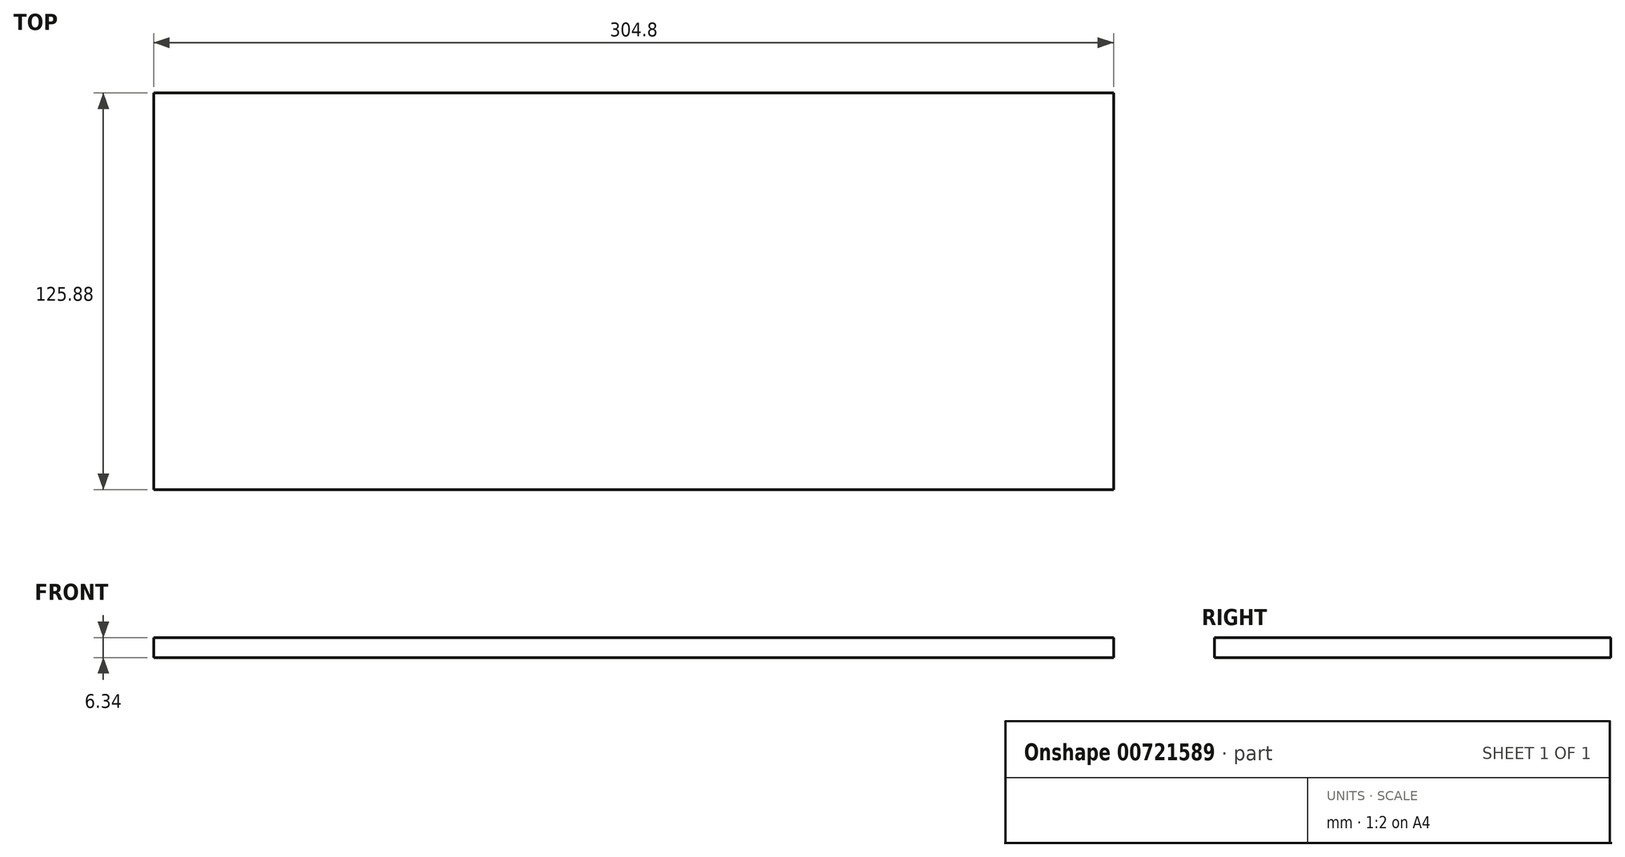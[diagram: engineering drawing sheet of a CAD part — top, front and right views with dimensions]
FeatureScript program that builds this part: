
annotation { "Feature Type Name" : "Feature", "Feature Type Description" : "" }
export const myFeature = defineFeature(function(context is Context, id is Id, definition is map)
    precondition{}
    {
        {
            var Q0;
            Q0=qCreatedBy(makeId("Top.planeOp"),FACE);
            var sketch = newSketch(context, id + "F0", { "sketchPlane" : qUnion([Q0])});
            skLineSegment(sketch, "E0.bottom", {"start": v(152.4, -62.94) * mm, "end": v(-152.4, -62.94) * mm});
            skLineSegment(sketch, "E0.top", {"start": v(152.4, 62.94) * mm, "end": v(-152.4, 62.94) * mm});
            skLineSegment(sketch, "E0.left", {"start": v(152.4, -62.94) * mm, "end": v(152.4, 62.94) * mm});
            skLineSegment(sketch, "E0.right", {"start": v(-152.4, -62.94) * mm, "end": v(-152.4, 62.94) * mm});
            skPoint(sketch, "E0.middle", {"position": v(0, 0) * mm});
            skSolve(sketch);
        }
        {
            var Q0;
            Q0=makeQuery(id+"F0.imprint","IMPRINT",FACE,{"disambiguationData":[TD([[makeQuery(id+"F0.imprint","IMPRINT",EDGE,{"derivedFrom":sQuery(id+"F0.wireOp",EDGE,"E0.bottom")}),-1.0]])]});
            extrude(context, id + "F1", {"entities" : qUnion([Q0]), "depth" : 6.35 * mm, "offsetDistance" : 25.4 * mm, "symmetric" : true});
        }
    });
